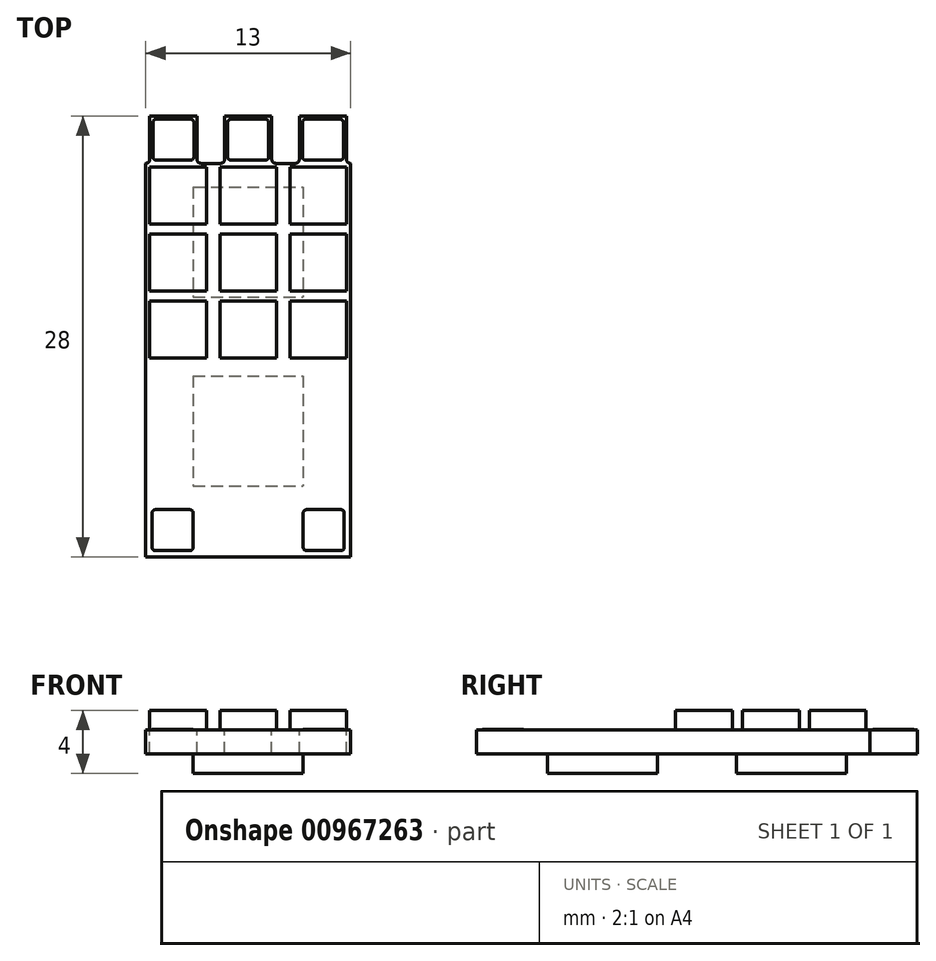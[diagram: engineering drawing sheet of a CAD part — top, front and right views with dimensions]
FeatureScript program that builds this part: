
annotation { "Feature Type Name" : "Feature", "Feature Type Description" : "" }
export const myFeature = defineFeature(function(context is Context, id is Id, definition is map)
    precondition{}
    {
        {
            var Q0;
            Q0=qCreatedBy(makeId("Top.planeOp"),FACE);
            var sketch = newSketch(context, id + "F0", { "sketchPlane" : qUnion([Q0])});
            skLineSegment(sketch, "E0.bottom", {"start": v(-6.5, 14) * mm, "end": v(6.5, 14) * mm});
            skLineSegment(sketch, "E0.top", {"start": v(-6.5, -14) * mm, "end": v(6.5, -14) * mm});
            skLineSegment(sketch, "E0.left", {"start": v(-6.5, 14) * mm, "end": v(-6.5, -14) * mm});
            skLineSegment(sketch, "E0.right", {"start": v(6.5, 14) * mm, "end": v(6.5, -14) * mm});
            skSolve(sketch);
        }
        {
            var Q0;
            Q0=makeQuery(id+"F0.imprint","IMPRINT",FACE,{"disambiguationData":[TD([[makeQuery(id+"F0.imprint","IMPRINT",EDGE,{"derivedFrom":sQuery(id+"F0.wireOp",EDGE,"E0.bottom")}),-1.0]])]});
            extrude(context, id + "F1", {"entities" : qUnion([Q0]), "depth" : 1.5 * mm});
        }
        {
            var Q0;
            Q0=makeQuery(id+"F1.opExtrude","CAP_FACE",FACE,{"disambiguationData":[OSD([sQuery(id+"F0.wireOp",EDGE,"E0.bottom"),sQuery(id+"F0.wireOp",EDGE,"E0.top"),sQuery(id+"F0.wireOp",EDGE,"E0.left"),sQuery(id+"F0.wireOp",EDGE,"E0.right")])],"isStart":false});
            var sketch = newSketch(context, id + "F2", { "sketchPlane" : qUnion([Q0])});
            skLineSegment(sketch, "E1.bottom", {"start": v(-3.25, 14) * mm, "end": v(-1.5, 14) * mm});
            skLineSegment(sketch, "E1.top", {"start": v(-3.25, 11) * mm, "end": v(-1.5, 11) * mm});
            skLineSegment(sketch, "E1.left", {"start": v(-3.25, 14) * mm, "end": v(-3.25, 11) * mm});
            skLineSegment(sketch, "E1.right", {"start": v(-1.5, 14) * mm, "end": v(-1.5, 11) * mm});
            skLineSegment(sketch, "E2.bottom", {"start": v(1.5, 14) * mm, "end": v(3.25, 14) * mm});
            skLineSegment(sketch, "E2.top", {"start": v(1.5, 11) * mm, "end": v(3.25, 11) * mm});
            skLineSegment(sketch, "E2.left", {"start": v(1.5, 14) * mm, "end": v(1.5, 11) * mm});
            skLineSegment(sketch, "E2.right", {"start": v(3.25, 14) * mm, "end": v(3.25, 11) * mm});
            skLineSegment(sketch, "E3.bottom", {"start": v(-6.5, 14) * mm, "end": v(-6.25, 14) * mm});
            skLineSegment(sketch, "E3.top", {"start": v(-6.5, 11) * mm, "end": v(-6.25, 11) * mm});
            skLineSegment(sketch, "E3.left", {"start": v(-6.5, 14) * mm, "end": v(-6.5, 11) * mm});
            skLineSegment(sketch, "E3.right", {"start": v(-6.25, 14) * mm, "end": v(-6.25, 11) * mm});
            skPoint(sketch, "E4.oppositeSnap0", {"position": v(-2.38, 11) * mm});
            skLineSegment(sketch, "E4.bottom", {"start": v(6.5, 14) * mm, "end": v(6.25, 14) * mm});
            skLineSegment(sketch, "E4.top", {"start": v(6.5, 11) * mm, "end": v(6.25, 11) * mm});
            skLineSegment(sketch, "E4.left", {"start": v(6.5, 14) * mm, "end": v(6.5, 11) * mm});
            skLineSegment(sketch, "E4.right", {"start": v(6.25, 14) * mm, "end": v(6.25, 11) * mm});
            skSolve(sketch);
        }
        {
            var Q0;
            Q0=qSketchRegion(id+"F2",true);
            extrude(context, id + "F3", {"entities" : qUnion([Q0]), "operationType" : NewBodyOperationType.REMOVE, "oppositeDirection" : true, "depth" : 25 * mm});
        }
        {
            var Q0;
            Q0=makeQuery(id+"F1.opExtrude","CAP_FACE",FACE,{"disambiguationData":[OSD([sQuery(id+"F0.wireOp",EDGE,"E0.bottom"),sQuery(id+"F0.wireOp",EDGE,"E0.top"),sQuery(id+"F0.wireOp",EDGE,"E0.left"),sQuery(id+"F0.wireOp",EDGE,"E0.right")])],"isStart":false});
            var sketch = newSketch(context, id + "F4", { "sketchPlane" : qUnion([Q0])});
            skLineSegment(sketch, "E5.bottom", {"start": v(-6.05, 13.8) * mm, "end": v(-3.45, 13.8) * mm});
            skLineSegment(sketch, "E5.top", {"start": v(-6.05, 11.2) * mm, "end": v(-3.45, 11.2) * mm});
            skLineSegment(sketch, "E5.left", {"start": v(-6.05, 13.8) * mm, "end": v(-6.05, 11.2) * mm});
            skLineSegment(sketch, "E5.right", {"start": v(-3.45, 13.8) * mm, "end": v(-3.45, 11.2) * mm});
            skLineSegment(sketch, "E6.bottom", {"start": v(-1.3, 13.8) * mm, "end": v(1.3, 13.8) * mm});
            skLineSegment(sketch, "E6.top", {"start": v(-1.3, 11.2) * mm, "end": v(1.3, 11.2) * mm});
            skLineSegment(sketch, "E6.left", {"start": v(-1.3, 13.8) * mm, "end": v(-1.3, 11.2) * mm});
            skLineSegment(sketch, "E6.right", {"start": v(1.3, 13.8) * mm, "end": v(1.3, 11.2) * mm});
            skLineSegment(sketch, "E7.bottom", {"start": v(3.45, 13.8) * mm, "end": v(6.05, 13.8) * mm});
            skLineSegment(sketch, "E7.top", {"start": v(3.45, 11.2) * mm, "end": v(6.05, 11.2) * mm});
            skLineSegment(sketch, "E7.left", {"start": v(3.45, 13.8) * mm, "end": v(3.45, 11.2) * mm});
            skLineSegment(sketch, "E7.right", {"start": v(6.05, 13.8) * mm, "end": v(6.05, 11.2) * mm});
            skSolve(sketch);
        }
        {
            var Q0;
            Q0=makeQuery(id+"F4.imprint","IMPRINT",FACE,{"disambiguationData":[TD([[makeQuery(id+"F4.imprint","IMPRINT",EDGE,{"derivedFrom":sQuery(id+"F4.wireOp",EDGE,"E5.bottom")}),-1.0]])]});
            var Q1;
            Q1=makeQuery(id+"F4.imprint","IMPRINT",FACE,{"disambiguationData":[TD([[makeQuery(id+"F4.imprint","IMPRINT",EDGE,{"derivedFrom":sQuery(id+"F4.wireOp",EDGE,"E6.bottom")}),-1.0]])]});
            var Q2;
            Q2=makeQuery(id+"F4.imprint","IMPRINT",FACE,{"disambiguationData":[TD([[makeQuery(id+"F4.imprint","IMPRINT",EDGE,{"derivedFrom":sQuery(id+"F4.wireOp",EDGE,"E7.bottom")}),-1.0]])]});
            extrude(context, id + "F5", {"entities" : qUnion([Q0, Q1, Q2]), "operationType" : NewBodyOperationType.ADD, "depth" : 0.05 * mm});
        }
        {
            var Q0;
            Q0=makeQuery(id+"F5.opExtrude","SWEPT_EDGE",EDGE,{"disambiguationData":[OSD([sQuery(id+"F4.wireOp",EDGE,"E5.top"),sQuery(id+"F4.wireOp",EDGE,"E5.left")])]});
            var Q1;
            Q1=makeQuery(id+"F5.opExtrude","SWEPT_EDGE",EDGE,{"disambiguationData":[OSD([sQuery(id+"F4.wireOp",EDGE,"E5.bottom"),sQuery(id+"F4.wireOp",EDGE,"E5.left")])]});
            var Q2;
            Q2=makeQuery(id+"F5.opExtrude","SWEPT_EDGE",EDGE,{"disambiguationData":[OSD([sQuery(id+"F4.wireOp",EDGE,"E5.top"),sQuery(id+"F4.wireOp",EDGE,"E5.right")])]});
            var Q3;
            Q3=makeQuery(id+"F5.opExtrude","SWEPT_EDGE",EDGE,{"disambiguationData":[OSD([sQuery(id+"F4.wireOp",EDGE,"E5.bottom"),sQuery(id+"F4.wireOp",EDGE,"E5.right")])]});
            var Q4;
            Q4=makeQuery(id+"F5.opExtrude","SWEPT_EDGE",EDGE,{"disambiguationData":[OSD([sQuery(id+"F4.wireOp",EDGE,"E6.bottom"),sQuery(id+"F4.wireOp",EDGE,"E6.right")])]});
            var Q5;
            Q5=makeQuery(id+"F5.opExtrude","SWEPT_EDGE",EDGE,{"disambiguationData":[OSD([sQuery(id+"F4.wireOp",EDGE,"E6.bottom"),sQuery(id+"F4.wireOp",EDGE,"E6.left")])]});
            var Q6;
            Q6=makeQuery(id+"F5.opExtrude","SWEPT_EDGE",EDGE,{"disambiguationData":[OSD([sQuery(id+"F4.wireOp",EDGE,"E6.top"),sQuery(id+"F4.wireOp",EDGE,"E6.right")])]});
            var Q7;
            Q7=makeQuery(id+"F5.opExtrude","SWEPT_EDGE",EDGE,{"disambiguationData":[OSD([sQuery(id+"F4.wireOp",EDGE,"E7.bottom"),sQuery(id+"F4.wireOp",EDGE,"E7.left")])]});
            var Q8;
            Q8=makeQuery(id+"F5.opExtrude","SWEPT_EDGE",EDGE,{"disambiguationData":[OSD([sQuery(id+"F4.wireOp",EDGE,"E7.bottom"),sQuery(id+"F4.wireOp",EDGE,"E7.right")])]});
            var Q9;
            Q9=makeQuery(id+"F5.opExtrude","SWEPT_EDGE",EDGE,{"disambiguationData":[OSD([sQuery(id+"F4.wireOp",EDGE,"E7.top"),sQuery(id+"F4.wireOp",EDGE,"E7.right")])]});
            var Q10;
            Q10=makeQuery(id+"F5.opExtrude","SWEPT_EDGE",EDGE,{"disambiguationData":[OSD([sQuery(id+"F4.wireOp",EDGE,"E6.top"),sQuery(id+"F4.wireOp",EDGE,"E6.left")])]});
            var Q11;
            Q11=makeQuery(id+"F5.opExtrude","SWEPT_EDGE",EDGE,{"disambiguationData":[OSD([sQuery(id+"F4.wireOp",EDGE,"E7.top"),sQuery(id+"F4.wireOp",EDGE,"E7.left")])]});
            fillet(context, id + "F6", {"entities" : qUnion([Q0, Q1, Q2, Q3, Q4, Q5, Q6, Q7, Q8, Q9, Q10, Q11]), "radius" : 0.2 * mm, "tangentPropagation" : true, "allowEdgeOverflow" : false});
        }
        {
            var Q0;
            Q0=makeQuery(id+"F3.boolean.opBoolean","COPY",EDGE,{"derivedFrom":makeQuery(id+"F3.opExtrude","SWEPT_EDGE",EDGE,{"disambiguationData":[OSD([sQuery(id+"F2.wireOp",EDGE,"E4.top"),sQuery(id+"F2.wireOp",EDGE,"E4.right")])]})});
            var Q1;
            Q1=makeQuery(id+"F3.boolean.opBoolean","COPY",EDGE,{"derivedFrom":makeQuery(id+"F3.opExtrude","SWEPT_EDGE",EDGE,{"disambiguationData":[OSD([sQuery(id+"F2.wireOp",EDGE,"E3.top"),sQuery(id+"F2.wireOp",EDGE,"E3.right")])]})});
            var Q2;
            Q2=makeQuery(id+"F3.boolean.opBoolean","COPY",EDGE,{"derivedFrom":makeQuery(id+"F3.opExtrude","SWEPT_EDGE",EDGE,{"disambiguationData":[OSD([sQuery(id+"F2.wireOp",EDGE,"E1.top"),sQuery(id+"F2.wireOp",EDGE,"E1.right")])]})});
            var Q3;
            Q3=makeQuery(id+"F3.boolean.opBoolean","COPY",EDGE,{"derivedFrom":makeQuery(id+"F3.opExtrude","SWEPT_EDGE",EDGE,{"disambiguationData":[OSD([sQuery(id+"F2.wireOp",EDGE,"E2.top"),sQuery(id+"F2.wireOp",EDGE,"E2.right")])]})});
            var Q4;
            Q4=makeQuery(id+"F3.boolean.opBoolean","COPY",EDGE,{"derivedFrom":makeQuery(id+"F3.opExtrude","SWEPT_EDGE",EDGE,{"disambiguationData":[OSD([sQuery(id+"F2.wireOp",EDGE,"E1.top"),sQuery(id+"F2.wireOp",EDGE,"E1.left")])]})});
            var Q5;
            Q5=makeQuery(id+"F3.boolean.opBoolean","COPY",EDGE,{"derivedFrom":makeQuery(id+"F3.opExtrude","SWEPT_EDGE",EDGE,{"disambiguationData":[OSD([sQuery(id+"F2.wireOp",EDGE,"E2.top"),sQuery(id+"F2.wireOp",EDGE,"E2.left")])]})});
            fillet(context, id + "F7", {"entities" : qUnion([Q0, Q1, Q2, Q3, Q4, Q5]), "radius" : 0.25 * mm, "tangentPropagation" : true, "allowEdgeOverflow" : false});
        }
        {
            var Q0;
            Q0=makeQuery(id+"F1.opExtrude","CAP_FACE",FACE,{"disambiguationData":[OSD([sQuery(id+"F0.wireOp",EDGE,"E0.bottom"),sQuery(id+"F0.wireOp",EDGE,"E0.top"),sQuery(id+"F0.wireOp",EDGE,"E0.left"),sQuery(id+"F0.wireOp",EDGE,"E0.right")])],"isStart":false});
            var sketch = newSketch(context, id + "F8", { "sketchPlane" : qUnion([Q0])});
            skLineSegment(sketch, "E8.bottom", {"start": v(-6.1, -11) * mm, "end": v(-3.5, -11) * mm});
            skLineSegment(sketch, "E8.top", {"start": v(-6.1, -13.6) * mm, "end": v(-3.5, -13.6) * mm});
            skLineSegment(sketch, "E8.left", {"start": v(-6.1, -11) * mm, "end": v(-6.1, -13.6) * mm});
            skLineSegment(sketch, "E8.right", {"start": v(-3.5, -11) * mm, "end": v(-3.5, -13.6) * mm});
            skLineSegment(sketch, "E9.bottom", {"start": v(3.5, -11) * mm, "end": v(6.1, -11) * mm});
            skLineSegment(sketch, "E9.top", {"start": v(3.5, -13.6) * mm, "end": v(6.1, -13.6) * mm});
            skLineSegment(sketch, "E9.left", {"start": v(3.5, -11) * mm, "end": v(3.5, -13.6) * mm});
            skLineSegment(sketch, "E9.right", {"start": v(6.1, -11) * mm, "end": v(6.1, -13.6) * mm});
            skSolve(sketch);
        }
        {
            var Q0;
            Q0=makeQuery(id+"F8.imprint","IMPRINT",FACE,{"disambiguationData":[TD([[makeQuery(id+"F8.imprint","IMPRINT",EDGE,{"derivedFrom":sQuery(id+"F8.wireOp",EDGE,"E8.bottom")}),-1.0]])]});
            var Q1;
            Q1=makeQuery(id+"F8.imprint","IMPRINT",FACE,{"disambiguationData":[TD([[makeQuery(id+"F8.imprint","IMPRINT",EDGE,{"derivedFrom":sQuery(id+"F8.wireOp",EDGE,"E9.bottom")}),-1.0]])]});
            extrude(context, id + "F9", {"entities" : qUnion([Q0, Q1]), "operationType" : NewBodyOperationType.ADD, "depth" : 0.05 * mm});
        }
        {
            var Q0;
            Q0=makeQuery(id+"F9.opExtrude","SWEPT_EDGE",EDGE,{"disambiguationData":[OSD([sQuery(id+"F8.wireOp",EDGE,"E8.top"),sQuery(id+"F8.wireOp",EDGE,"E8.left")])]});
            var Q1;
            Q1=makeQuery(id+"F9.opExtrude","SWEPT_EDGE",EDGE,{"disambiguationData":[OSD([sQuery(id+"F8.wireOp",EDGE,"E8.top"),sQuery(id+"F8.wireOp",EDGE,"E8.right")])]});
            var Q2;
            Q2=makeQuery(id+"F9.opExtrude","SWEPT_EDGE",EDGE,{"disambiguationData":[OSD([sQuery(id+"F8.wireOp",EDGE,"E8.bottom"),sQuery(id+"F8.wireOp",EDGE,"E8.left")])]});
            var Q3;
            Q3=makeQuery(id+"F9.opExtrude","SWEPT_EDGE",EDGE,{"disambiguationData":[OSD([sQuery(id+"F8.wireOp",EDGE,"E9.top"),sQuery(id+"F8.wireOp",EDGE,"E9.left")])]});
            var Q4;
            Q4=makeQuery(id+"F9.opExtrude","SWEPT_EDGE",EDGE,{"disambiguationData":[OSD([sQuery(id+"F8.wireOp",EDGE,"E9.top"),sQuery(id+"F8.wireOp",EDGE,"E9.right")])]});
            var Q5;
            Q5=makeQuery(id+"F9.opExtrude","SWEPT_EDGE",EDGE,{"disambiguationData":[OSD([sQuery(id+"F8.wireOp",EDGE,"E9.bottom"),sQuery(id+"F8.wireOp",EDGE,"E9.left")])]});
            var Q6;
            Q6=makeQuery(id+"F9.opExtrude","SWEPT_EDGE",EDGE,{"disambiguationData":[OSD([sQuery(id+"F8.wireOp",EDGE,"E8.bottom"),sQuery(id+"F8.wireOp",EDGE,"E8.right")])]});
            var Q7;
            Q7=makeQuery(id+"F9.opExtrude","SWEPT_EDGE",EDGE,{"disambiguationData":[OSD([sQuery(id+"F8.wireOp",EDGE,"E9.bottom"),sQuery(id+"F8.wireOp",EDGE,"E9.right")])]});
            fillet(context, id + "F10", {"entities" : qUnion([Q0, Q1, Q2, Q3, Q4, Q5, Q6, Q7]), "radius" : 0.2 * mm, "tangentPropagation" : true, "allowEdgeOverflow" : false});
        }
        {
            var Q0;
            Q0=makeQuery(id+"F1.opExtrude","CAP_FACE",FACE,{"disambiguationData":[OSD([sQuery(id+"F0.wireOp",EDGE,"E0.bottom"),sQuery(id+"F0.wireOp",EDGE,"E0.top"),sQuery(id+"F0.wireOp",EDGE,"E0.left"),sQuery(id+"F0.wireOp",EDGE,"E0.right")])],"isStart":false});
            var sketch = newSketch(context, id + "F11", { "sketchPlane" : qUnion([Q0])});
            skLineSegment(sketch, "E10.bottom", {"start": v(-6.25, 10.75) * mm, "end": v(-2.65, 10.75) * mm});
            skLineSegment(sketch, "E10.top", {"start": v(-6.25, 7.15) * mm, "end": v(-2.65, 7.15) * mm});
            skLineSegment(sketch, "E10.left", {"start": v(-6.25, 10.75) * mm, "end": v(-6.25, 7.15) * mm});
            skLineSegment(sketch, "E10.right", {"start": v(-2.65, 10.75) * mm, "end": v(-2.65, 7.15) * mm});
            skLineSegment(sketch, "E11.bottom", {"start": v(-1.8, 10.75) * mm, "end": v(1.8, 10.75) * mm});
            skLineSegment(sketch, "E11.top", {"start": v(-1.8, 7.15) * mm, "end": v(1.8, 7.15) * mm});
            skLineSegment(sketch, "E11.left", {"start": v(-1.8, 10.75) * mm, "end": v(-1.8, 7.15) * mm});
            skLineSegment(sketch, "E11.right", {"start": v(1.8, 10.75) * mm, "end": v(1.8, 7.15) * mm});
            skLineSegment(sketch, "E12.bottom", {"start": v(2.65, 10.75) * mm, "end": v(6.25, 10.75) * mm});
            skLineSegment(sketch, "E12.top", {"start": v(2.65, 7.15) * mm, "end": v(6.25, 7.15) * mm});
            skLineSegment(sketch, "E12.left", {"start": v(2.65, 10.75) * mm, "end": v(2.65, 7.15) * mm});
            skLineSegment(sketch, "E12.right", {"start": v(6.25, 10.75) * mm, "end": v(6.25, 7.15) * mm});
            skLineSegment(sketch, "E13.0.1.0", {"start": v(2.65, 2.9) * mm, "end": v(6.25, 2.9) * mm});
            skLineSegment(sketch, "E13.0.1.1", {"start": v(2.65, 6.5) * mm, "end": v(2.65, 2.9) * mm});
            skLineSegment(sketch, "E13.0.1.2", {"start": v(2.65, 6.5) * mm, "end": v(6.25, 6.5) * mm});
            skLineSegment(sketch, "E13.0.1.3", {"start": v(1.8, 6.5) * mm, "end": v(1.8, 2.9) * mm});
            skLineSegment(sketch, "E13.0.1.4", {"start": v(-1.8, 6.5) * mm, "end": v(-1.8, 2.9) * mm});
            skLineSegment(sketch, "E13.0.1.5", {"start": v(-1.8, 2.9) * mm, "end": v(1.8, 2.9) * mm});
            skLineSegment(sketch, "E13.0.1.6", {"start": v(6.25, 6.5) * mm, "end": v(6.25, 2.9) * mm});
            skLineSegment(sketch, "E13.0.1.7", {"start": v(-1.8, 6.5) * mm, "end": v(1.8, 6.5) * mm});
            skLineSegment(sketch, "E13.0.1.8", {"start": v(-2.65, 6.5) * mm, "end": v(-2.65, 2.9) * mm});
            skLineSegment(sketch, "E13.0.1.9", {"start": v(-6.25, 6.5) * mm, "end": v(-6.25, 2.9) * mm});
            skLineSegment(sketch, "E13.0.1.10", {"start": v(-6.25, 2.9) * mm, "end": v(-2.65, 2.9) * mm});
            skLineSegment(sketch, "E13.0.1.11", {"start": v(-6.25, 6.5) * mm, "end": v(-2.65, 6.5) * mm});
            skLineSegment(sketch, "E13.0.2.0", {"start": v(2.65, -1.35) * mm, "end": v(6.25, -1.35) * mm});
            skLineSegment(sketch, "E13.0.2.1", {"start": v(2.65, 2.25) * mm, "end": v(2.65, -1.35) * mm});
            skLineSegment(sketch, "E13.0.2.2", {"start": v(2.65, 2.25) * mm, "end": v(6.25, 2.25) * mm});
            skLineSegment(sketch, "E13.0.2.3", {"start": v(1.8, 2.25) * mm, "end": v(1.8, -1.35) * mm});
            skLineSegment(sketch, "E13.0.2.4", {"start": v(-1.8, 2.25) * mm, "end": v(-1.8, -1.35) * mm});
            skLineSegment(sketch, "E13.0.2.5", {"start": v(-1.8, -1.35) * mm, "end": v(1.8, -1.35) * mm});
            skLineSegment(sketch, "E13.0.2.6", {"start": v(6.25, 2.25) * mm, "end": v(6.25, -1.35) * mm});
            skLineSegment(sketch, "E13.0.2.7", {"start": v(-1.8, 2.25) * mm, "end": v(1.8, 2.25) * mm});
            skLineSegment(sketch, "E13.0.2.8", {"start": v(-2.65, 2.25) * mm, "end": v(-2.65, -1.35) * mm});
            skLineSegment(sketch, "E13.0.2.9", {"start": v(-6.25, 2.25) * mm, "end": v(-6.25, -1.35) * mm});
            skLineSegment(sketch, "E13.0.2.10", {"start": v(-6.25, -1.35) * mm, "end": v(-2.65, -1.35) * mm});
            skLineSegment(sketch, "E13.0.2.11", {"start": v(-6.25, 2.25) * mm, "end": v(-2.65, 2.25) * mm});
            skLineSegment(sketch, "E13.direction1", {"start": v(-6.25, 7.15) * mm, "end": v(18.75, 7.15) * mm, "construction": true});
            skLineSegment(sketch, "E13.direction2", {"start": v(-6.25, 7.15) * mm, "end": v(-6.25, 2.9) * mm, "construction": true});
            skSolve(sketch);
        }
        {
            var Q0;
            Q0=qSketchRegion(id+"F11",true);
            extrude(context, id + "F12", {"entities" : qUnion([Q0]), "operationType" : NewBodyOperationType.ADD, "depth" : 1.25 * mm});
        }
        {
            var Q0;
            Q0=makeQuery(id+"F1.opExtrude","CAP_FACE",FACE,{"disambiguationData":[OSD([sQuery(id+"F0.wireOp",EDGE,"E0.bottom"),sQuery(id+"F0.wireOp",EDGE,"E0.top"),sQuery(id+"F0.wireOp",EDGE,"E0.left"),sQuery(id+"F0.wireOp",EDGE,"E0.right")])],"isStart":true});
            var sketch = newSketch(context, id + "F13", { "sketchPlane" : qUnion([Q0])});
            skLineSegment(sketch, "E14.bottom", {"start": v(-3.5, -9.5) * mm, "end": v(3.5, -9.5) * mm});
            skLineSegment(sketch, "E14.top", {"start": v(-3.5, -2.5) * mm, "end": v(3.5, -2.5) * mm});
            skLineSegment(sketch, "E14.left", {"start": v(-3.5, -9.5) * mm, "end": v(-3.5, -2.5) * mm});
            skLineSegment(sketch, "E14.right", {"start": v(3.5, -9.5) * mm, "end": v(3.5, -2.5) * mm});
            skLineSegment(sketch, "E15.bottom", {"start": v(-3.5, 2.5) * mm, "end": v(3.5, 2.5) * mm});
            skLineSegment(sketch, "E15.top", {"start": v(-3.5, 9.5) * mm, "end": v(3.5, 9.5) * mm});
            skLineSegment(sketch, "E15.left", {"start": v(-3.5, 2.5) * mm, "end": v(-3.5, 9.5) * mm});
            skLineSegment(sketch, "E15.right", {"start": v(3.5, 2.5) * mm, "end": v(3.5, 9.5) * mm});
            skSolve(sketch);
        }
        {
            var Q0;
            Q0=qSketchRegion(id+"F13",true);
            extrude(context, id + "F14", {"entities" : qUnion([Q0]), "operationType" : NewBodyOperationType.ADD, "depth" : 1.25 * mm});
        }
    });
